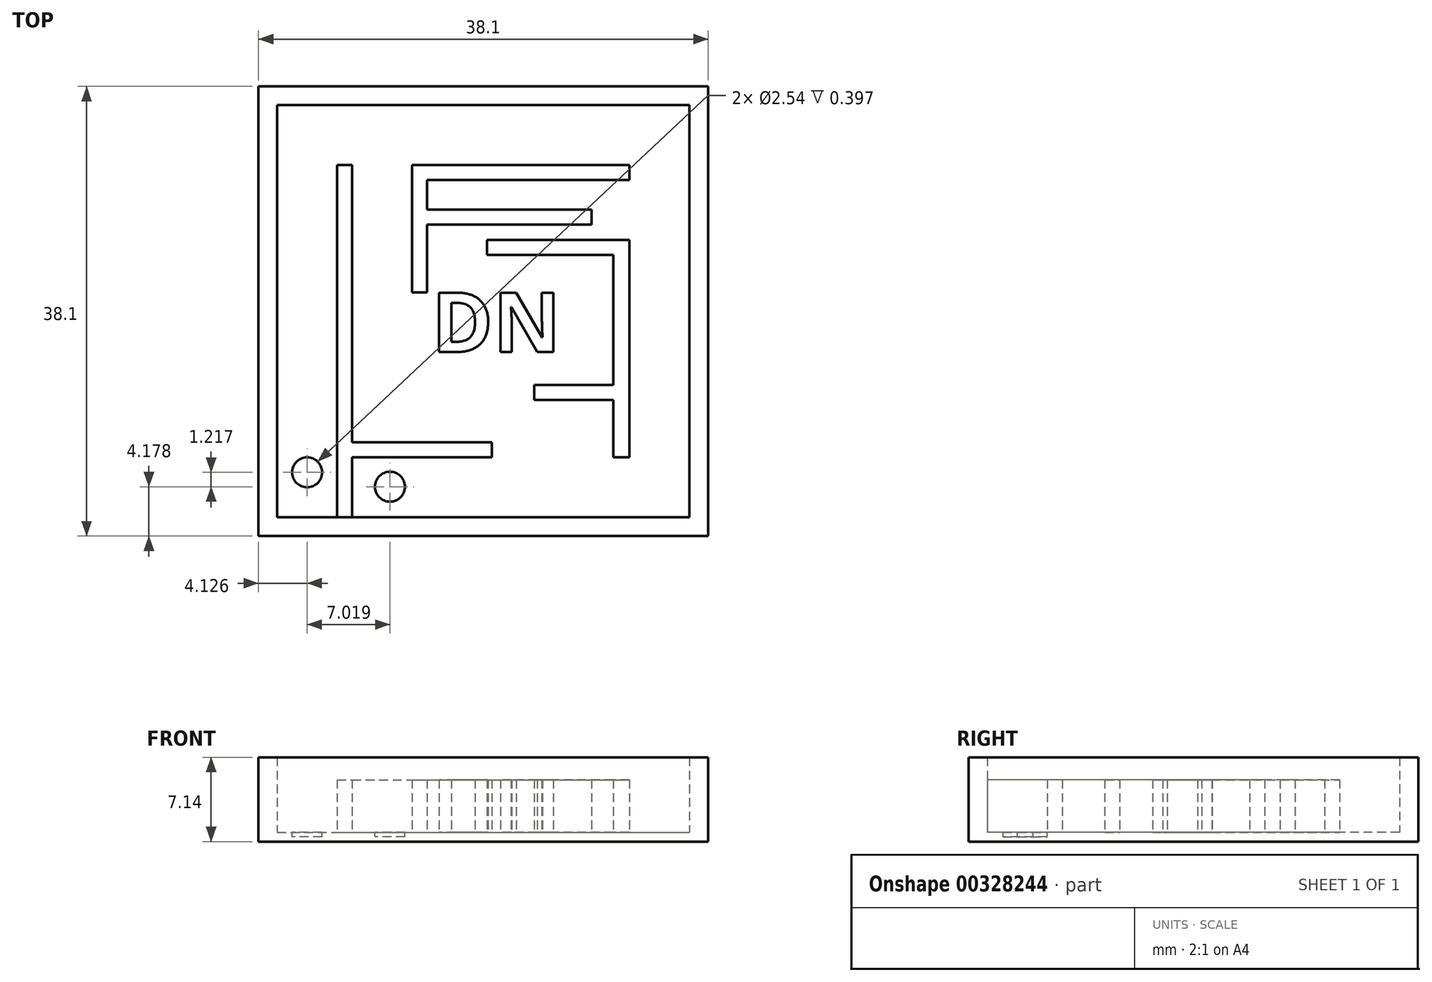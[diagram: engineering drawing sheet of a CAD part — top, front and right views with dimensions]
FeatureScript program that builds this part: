
annotation { "Feature Type Name" : "Feature", "Feature Type Description" : "" }
export const myFeature = defineFeature(function(context is Context, id is Id, definition is map)
    precondition{}
    {
        {
            var Q0;
            Q0=qCreatedBy(makeId("Top.planeOp"),FACE);
            var sketch = newSketch(context, id + "F0", { "sketchPlane" : qUnion([Q0])});
            skLineSegment(sketch, "E0.bottom", {"start": v(-18.83, 21.98) * mm, "end": v(19.27, 21.98) * mm});
            skLineSegment(sketch, "E0.top", {"start": v(-18.83, -16.12) * mm, "end": v(19.27, -16.12) * mm});
            skLineSegment(sketch, "E0.left", {"start": v(-18.83, 21.98) * mm, "end": v(-18.83, -16.12) * mm});
            skLineSegment(sketch, "E0.right", {"start": v(19.27, 21.98) * mm, "end": v(19.27, -16.12) * mm});
            skSolve(sketch);
        }
        {
            var Q0;
            Q0=makeQuery(id+"F0.imprint","IMPRINT",FACE,{"disambiguationData":[TD([[makeQuery(id+"F0.imprint","IMPRINT",EDGE,{"derivedFrom":sQuery(id+"F0.wireOp",EDGE,"E0.bottom")}),-1.0]])]});
            extrude(context, id + "F1", {"entities" : qUnion([Q0]), "depth" : 0.8 * mm});
        }
        {
            var Q0;
            Q0=makeQuery(id+"F1.opExtrude","CAP_FACE",FACE,{"disambiguationData":[OSD([sQuery(id+"F0.wireOp",EDGE,"E0.bottom"),sQuery(id+"F0.wireOp",EDGE,"E0.top"),sQuery(id+"F0.wireOp",EDGE,"E0.left"),sQuery(id+"F0.wireOp",EDGE,"E0.right")])],"isStart":false});
            var sketch = newSketch(context, id + "F2", { "sketchPlane" : qUnion([Q0])});
            skLineSegment(sketch, "E1.0", {"start": v(-17.24, 20.39) * mm, "end": v(17.68, 20.39) * mm});
            skLineSegment(sketch, "E1.1", {"start": v(-17.24, 20.39) * mm, "end": v(-17.24, -14.54) * mm});
            skLineSegment(sketch, "E1.2", {"start": v(-17.24, -14.54) * mm, "end": v(17.68, -14.54) * mm});
            skLineSegment(sketch, "E1.3", {"start": v(17.68, 20.39) * mm, "end": v(17.68, -14.54) * mm});
            skSolve(sketch);
        }
        {
            var Q0;
            Q0=makeQuery(id+"F2.imprint","IMPRINT",FACE,{"disambiguationData":[TD([[makeQuery(id+"F2.imprint","IMPRINT",EDGE,{"derivedFrom":sQuery(id+"F2.wireOp",EDGE,"E1.0")}),1.0]])]});
            extrude(context, id + "F3", {"entities" : qUnion([Q0]), "operationType" : NewBodyOperationType.ADD, "depth" : 6.35 * mm});
        }
        {
            var Q0;
            Q0=makeQuery(id+"F1.opExtrude","CAP_FACE",FACE,{"disambiguationData":[OSD([sQuery(id+"F0.wireOp",EDGE,"E0.bottom"),sQuery(id+"F0.wireOp",EDGE,"E0.top"),sQuery(id+"F0.wireOp",EDGE,"E0.left"),sQuery(id+"F0.wireOp",EDGE,"E0.right")])],"isStart":false});
            var sketch = newSketch(context, id + "F4", { "sketchPlane" : qUnion([Q0])});
            skLineSegment(sketch, "E2.bottom", {"start": v(-12.16, 15.3) * mm, "end": v(-10.9, 15.3) * mm});
            skLineSegment(sketch, "E2.top", {"start": v(-12.16, -14.54) * mm, "end": v(-10.9, -14.54) * mm});
            skLineSegment(sketch, "E2.left", {"start": v(-12.16, 15.3) * mm, "end": v(-12.16, -14.54) * mm});
            skLineSegment(sketch, "E2.right", {"start": v(-10.9, 15.3) * mm, "end": v(-10.9, -14.54) * mm});
            skSolve(sketch);
        }
        {
            var Q0;
            Q0=makeQuery(id+"F4.imprint","IMPRINT",FACE,{"disambiguationData":[TD([[makeQuery(id+"F4.imprint","IMPRINT",EDGE,{"derivedFrom":sQuery(id+"F4.wireOp",EDGE,"E2.bottom")}),-1.0]])]});
            extrude(context, id + "F5", {"entities" : qUnion([Q0]), "operationType" : NewBodyOperationType.ADD, "depth" : 4.44 * mm});
        }
        {
            var Q0;
            Q0=makeQuery(id+"F1.opExtrude","CAP_FACE",FACE,{"disambiguationData":[OSD([sQuery(id+"F0.wireOp",EDGE,"E0.bottom"),sQuery(id+"F0.wireOp",EDGE,"E0.top"),sQuery(id+"F0.wireOp",EDGE,"E0.left"),sQuery(id+"F0.wireOp",EDGE,"E0.right")])],"isStart":false});
            var sketch = newSketch(context, id + "F6", { "sketchPlane" : qUnion([Q0])});
            skText(sketch, "E3", { "text": "DN", "fontName": "OpenSans-Bold.ttf"});
            const initialGuessF6  = {"E3": [-0.00418, -0.00054, 1, 0, 0.00508]};
            skSetInitialGuess(sketch, initialGuessF6);
            skSolve(sketch);
        }
        {
            var Q0;
            Q0 = qSketchRegion(id + "F6", true);
            extrude(context, id + "F7", {"entities" : qUnion([Q0]), "operationType" : NewBodyOperationType.ADD, "depth" : 4.44 * mm});
        }
        {
            var Q0;
            Q0=makeQuery(id+"F7.boolean.opBoolean","SPLIT",FACE,{"disambiguationData":[TD([makeQuery(id+"F3.opExtrude","SWEPT_FACE",FACE,{"disambiguationData":[OSD([sQuery(id+"F2.wireOp",EDGE,"E1.0")])]})])],"derivedFrom":makeQuery(id+"F1.opExtrude","CAP_FACE",FACE,{"disambiguationData":[OSD([sQuery(id+"F0.wireOp",EDGE,"E0.bottom"),sQuery(id+"F0.wireOp",EDGE,"E0.top"),sQuery(id+"F0.wireOp",EDGE,"E0.left"),sQuery(id+"F0.wireOp",EDGE,"E0.right")])],"isStart":false})});
            var sketch = newSketch(context, id + "F8", { "sketchPlane" : qUnion([Q0])});
            skLineSegment(sketch, "E4.bottom", {"start": v(-5.81, 4.52) * mm, "end": v(-4.54, 4.52) * mm});
            skLineSegment(sketch, "E4.left", {"start": v(-5.81, 4.52) * mm, "end": v(-5.81, 15.3) * mm});
            skLineSegment(sketch, "E4.right", {"start": v(-4.54, 4.52) * mm, "end": v(-4.54, 14.03) * mm});
            skLineSegment(sketch, "E5.top", {"start": v(-4.54, 14.03) * mm, "end": v(12.6, 14.03) * mm});
            skLineSegment(sketch, "E5.right", {"start": v(12.6, 15.3) * mm, "end": v(12.6, 14.03) * mm});
            skLineSegment(sketch, "E6", {"start": v(-5.81, 15.3) * mm, "end": v(12.6, 15.3) * mm});
            skSolve(sketch);
        }
        {
            var Q0;
            Q0 = qSketchRegion(id + "F8", true);
            extrude(context, id + "F9", {"entities" : qUnion([Q0]), "operationType" : NewBodyOperationType.ADD, "depth" : 4.44 * mm});
        }
        {
            var Q0;
            Q0=makeQuery(id+"F7.boolean.opBoolean","SPLIT",FACE,{"disambiguationData":[TD([makeQuery(id+"F3.opExtrude","SWEPT_FACE",FACE,{"disambiguationData":[OSD([sQuery(id+"F2.wireOp",EDGE,"E1.0")])]})])],"derivedFrom":makeQuery(id+"F1.opExtrude","CAP_FACE",FACE,{"disambiguationData":[OSD([sQuery(id+"F0.wireOp",EDGE,"E0.bottom"),sQuery(id+"F0.wireOp",EDGE,"E0.top"),sQuery(id+"F0.wireOp",EDGE,"E0.left"),sQuery(id+"F0.wireOp",EDGE,"E0.right")])],"isStart":false})});
            var sketch = newSketch(context, id + "F10", { "sketchPlane" : qUnion([Q0])});
            skLineSegment(sketch, "E7.bottom", {"start": v(0.54, 8.95) * mm, "end": v(12.6, 8.95) * mm});
            skLineSegment(sketch, "E7.top", {"start": v(0.54, 7.68) * mm, "end": v(11.23, 7.68) * mm});
            skLineSegment(sketch, "E7.left", {"start": v(0.54, 8.95) * mm, "end": v(0.54, 7.68) * mm});
            skLineSegment(sketch, "E7.right", {"start": v(12.6, 8.95) * mm, "end": v(12.6, 7.68) * mm});
            skLineSegment(sketch, "E8.top", {"start": v(12.6, -9.46) * mm, "end": v(11.23, -9.46) * mm});
            skLineSegment(sketch, "E8.left", {"start": v(12.6, 7.68) * mm, "end": v(12.6, -9.46) * mm});
            skLineSegment(sketch, "E8.right", {"start": v(11.23, 7.68) * mm, "end": v(11.23, -9.46) * mm});
            skSolve(sketch);
        }
        {
            var Q0;
            Q0 = qSketchRegion(id + "F10", true);
            extrude(context, id + "F11", {"entities" : qUnion([Q0]), "operationType" : NewBodyOperationType.ADD, "depth" : 4.44 * mm});
        }
        {
            var Q0;
            Q0=makeQuery(id+"F7.boolean.opBoolean","SPLIT",FACE,{"disambiguationData":[TD([makeQuery(id+"F3.opExtrude","SWEPT_FACE",FACE,{"disambiguationData":[OSD([sQuery(id+"F2.wireOp",EDGE,"E1.0")])]})])],"derivedFrom":makeQuery(id+"F1.opExtrude","CAP_FACE",FACE,{"disambiguationData":[OSD([sQuery(id+"F0.wireOp",EDGE,"E0.bottom"),sQuery(id+"F0.wireOp",EDGE,"E0.top"),sQuery(id+"F0.wireOp",EDGE,"E0.left"),sQuery(id+"F0.wireOp",EDGE,"E0.right")])],"isStart":false})});
            var sketch = newSketch(context, id + "F12", { "sketchPlane" : qUnion([Q0])});
            skCircle(sketch, "E9", {"center": v(-14.7, -10.73) * mm, "radius": 1.27 * mm});
            skPoint(sketch, "E9.centerSnap0", {"position": v(-14.7, -14.54) * mm});
            skSolve(sketch);
        }
        {
            var Q0;
            Q0 = qSketchRegion(id + "F12", true);
            extrude(context, id + "F13", {"entities" : qUnion([Q0]), "operationType" : NewBodyOperationType.REMOVE, "oppositeDirection" : true, "depth" : 0.4 * mm});
        }
        {
            var Q0;
            Q0=makeQuery(id+"F7.boolean.opBoolean","SPLIT",FACE,{"disambiguationData":[TD([makeQuery(id+"F3.opExtrude","SWEPT_FACE",FACE,{"disambiguationData":[OSD([sQuery(id+"F2.wireOp",EDGE,"E1.0")])]})])],"derivedFrom":makeQuery(id+"F1.opExtrude","CAP_FACE",FACE,{"disambiguationData":[OSD([sQuery(id+"F0.wireOp",EDGE,"E0.bottom"),sQuery(id+"F0.wireOp",EDGE,"E0.top"),sQuery(id+"F0.wireOp",EDGE,"E0.left"),sQuery(id+"F0.wireOp",EDGE,"E0.right")])],"isStart":false})});
            var sketch = newSketch(context, id + "F14", { "sketchPlane" : qUnion([Q0])});
            skLineSegment(sketch, "E10.bottom", {"start": v(-10.9, -4.5) * mm, "end": v(6.45, -4.5) * mm});
            skLineSegment(sketch, "E10.top", {"start": v(-10.9, -5.66) * mm, "end": v(6.45, -5.66) * mm});
            skLineSegment(sketch, "E10.right", {"start": v(6.45, -4.5) * mm, "end": v(6.45, -5.66) * mm});
            skLineSegment(sketch, "E11.bottom", {"start": v(-4.54, 11.52) * mm, "end": v(9.38, 11.52) * mm});
            skLineSegment(sketch, "E11.top", {"start": v(-4.54, 10.25) * mm, "end": v(9.38, 10.25) * mm});
            skLineSegment(sketch, "E11.right", {"start": v(9.38, 11.52) * mm, "end": v(9.38, 10.25) * mm});
            skPoint(sketch, "E12.bottom.start.orphan", {"position": v(3.4, 15.3) * mm});
            skLineSegment(sketch, "E13.bottom", {"start": v(-6.4, -12.53) * mm, "end": v(15.91, -12.53) * mm});
            skLineSegment(sketch, "E13.top", {"start": v(-6.4, -13.36) * mm, "end": v(15.91, -13.36) * mm});
            skLineSegment(sketch, "E13.left", {"start": v(-6.4, -12.53) * mm, "end": v(-6.4, -13.36) * mm});
            skLineSegment(sketch, "E13.right", {"start": v(15.91, -12.53) * mm, "end": v(15.91, -13.36) * mm});
            skSolve(sketch);
        }
        {
            var Q0;
            {var subQ0=sQuery(id+"F14.wireOp",EDGE,"E11.bottom");Q0=makeQuery(id+"F14.imprint","IMPRINT",FACE,{"disambiguationData":[TD([[makeQuery(id+"F14.imprint","IMPRINT",EDGE,{"derivedFrom":subQ0}),-1.0]])]});}
            extrude(context, id + "F15", {"entities" : qUnion([Q0]), "operationType" : NewBodyOperationType.ADD, "depth" : 4.44 * mm});
        }
        {
            var Q0;
            Q0=makeQuery(id+"F7.boolean.opBoolean","SPLIT",FACE,{"disambiguationData":[TD([makeQuery(id+"F3.opExtrude","SWEPT_FACE",FACE,{"disambiguationData":[OSD([sQuery(id+"F2.wireOp",EDGE,"E1.0")])]})])],"derivedFrom":makeQuery(id+"F1.opExtrude","CAP_FACE",FACE,{"disambiguationData":[OSD([sQuery(id+"F0.wireOp",EDGE,"E0.bottom"),sQuery(id+"F0.wireOp",EDGE,"E0.top"),sQuery(id+"F0.wireOp",EDGE,"E0.left"),sQuery(id+"F0.wireOp",EDGE,"E0.right")])],"isStart":false})});
            var sketch = newSketch(context, id + "F16", { "sketchPlane" : qUnion([Q0])});
            skLineSegment(sketch, "E14.bottom", {"start": v(-10.9, -8.19) * mm, "end": v(0.95, -8.19) * mm});
            skLineSegment(sketch, "E14.top", {"start": v(-10.9, -9.46) * mm, "end": v(0.95, -9.46) * mm});
            skLineSegment(sketch, "E14.right", {"start": v(0.95, -8.19) * mm, "end": v(0.95, -9.46) * mm});
            skCircle(sketch, "E15", {"center": v(-7.69, -11.94) * mm, "radius": 1.27 * mm});
            skPoint(sketch, "E16.orphan", {"position": v(-14.7, -10.73) * mm});
            skSolve(sketch);
        }
        {
            var Q0;
            Q0 = qSketchRegion(id + "F16", true);
            extrude(context, id + "F17", {"entities" : qUnion([Q0]), "operationType" : NewBodyOperationType.REMOVE, "oppositeDirection" : true, "depth" : 0.4 * mm});
        }
        {
            var Q0;
            {var subQ0=sQuery(id+"F16.wireOp",EDGE,"E14.bottom");Q0=makeQuery(id+"F16.imprint","IMPRINT",FACE,{"disambiguationData":[TD([[makeQuery(id+"F16.imprint","IMPRINT",EDGE,{"derivedFrom":subQ0}),-1.0]])]});}
            extrude(context, id + "F18", {"entities" : qUnion([Q0]), "operationType" : NewBodyOperationType.ADD, "depth" : 4.44 * mm});
        }
        {
            var Q0;
            Q0=makeQuery(id+"F7.boolean.opBoolean","SPLIT",FACE,{"disambiguationData":[TD([makeQuery(id+"F3.opExtrude","SWEPT_FACE",FACE,{"disambiguationData":[OSD([sQuery(id+"F2.wireOp",EDGE,"E1.0")])]})])],"derivedFrom":makeQuery(id+"F1.opExtrude","CAP_FACE",FACE,{"disambiguationData":[OSD([sQuery(id+"F0.wireOp",EDGE,"E0.bottom"),sQuery(id+"F0.wireOp",EDGE,"E0.top"),sQuery(id+"F0.wireOp",EDGE,"E0.left"),sQuery(id+"F0.wireOp",EDGE,"E0.right")])],"isStart":false})});
            var sketch = newSketch(context, id + "F19", { "sketchPlane" : qUnion([Q0])});
            skLineSegment(sketch, "E17.bottom", {"start": v(11.23, -4.58) * mm, "end": v(4.54, -4.58) * mm});
            skLineSegment(sketch, "E17.top", {"start": v(11.23, -3.31) * mm, "end": v(4.54, -3.31) * mm});
            skLineSegment(sketch, "E17.left", {"start": v(11.23, -4.58) * mm, "end": v(11.23, -3.31) * mm});
            skLineSegment(sketch, "E17.right", {"start": v(4.54, -4.58) * mm, "end": v(4.54, -3.31) * mm});
            skSolve(sketch);
        }
        {
            var Q0;
            Q0 = qSketchRegion(id + "F19", true);
            extrude(context, id + "F20", {"entities" : qUnion([Q0]), "operationType" : NewBodyOperationType.ADD, "depth" : 4.44 * mm});
        }
    });
